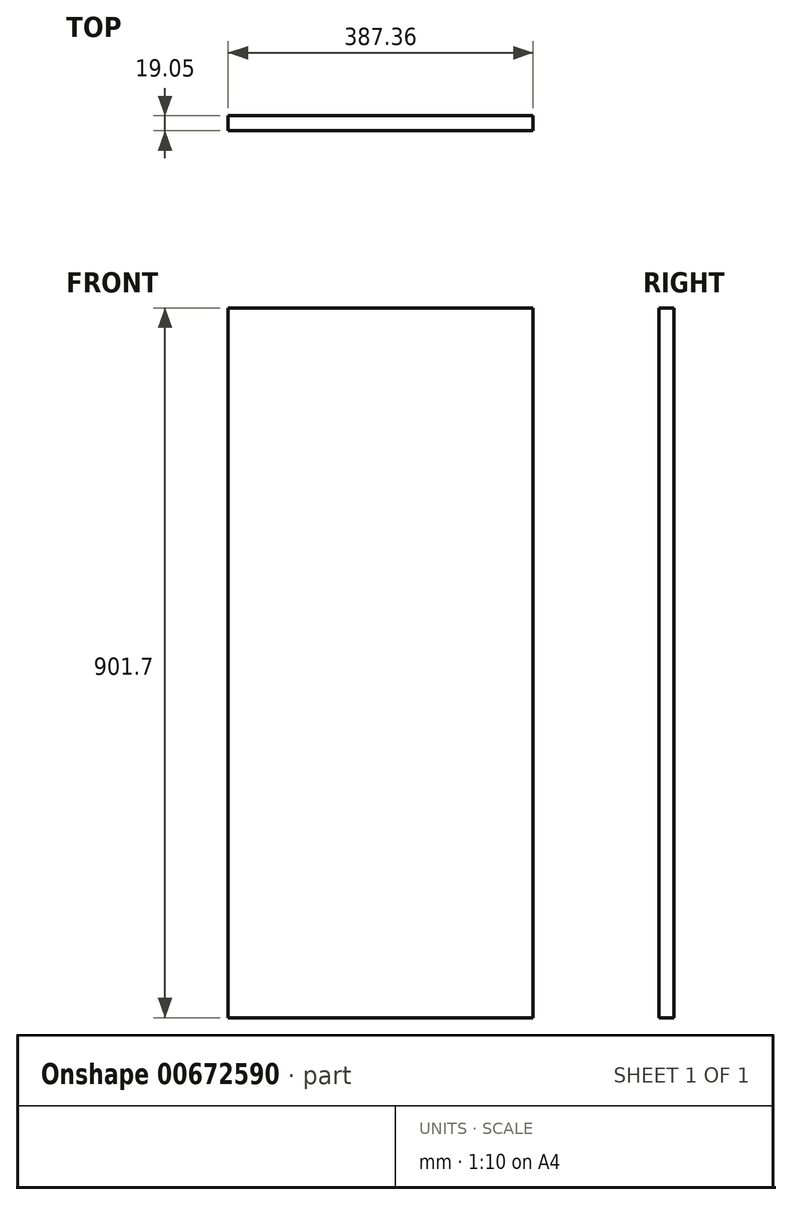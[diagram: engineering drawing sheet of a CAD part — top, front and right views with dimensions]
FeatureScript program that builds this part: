
annotation { "Feature Type Name" : "Feature", "Feature Type Description" : "" }
export const myFeature = defineFeature(function(context is Context, id is Id, definition is map)
    precondition{}
    {
        {
            var Q0;
            Q0=qCreatedBy(makeId("Front.planeOp"),FACE);
            var sketch = newSketch(context, id + "F0", { "sketchPlane" : qUnion([Q0])});
            skLineSegment(sketch, "E0.bottom", {"start": v(193.67, 450.85) * mm, "end": v(-193.68, 450.85) * mm});
            skLineSegment(sketch, "E0.top", {"start": v(193.68, -450.85) * mm, "end": v(-193.67, -450.85) * mm});
            skLineSegment(sketch, "E0.left", {"start": v(193.67, 450.85) * mm, "end": v(193.68, -450.85) * mm});
            skLineSegment(sketch, "E0.right", {"start": v(-193.68, 450.85) * mm, "end": v(-193.67, -450.85) * mm});
            skPoint(sketch, "E0.middle", {"position": v(0, 0) * mm});
            skSolve(sketch);
        }
        {
            var Q0;
            Q0=makeQuery(id+"F0.imprint","IMPRINT",FACE,{"disambiguationData":[TD([[makeQuery(id+"F0.imprint","IMPRINT",EDGE,{"derivedFrom":sQuery(id+"F0.wireOp",EDGE,"E0.bottom")}),1.0]])]});
            extrude(context, id + "F1", {"entities" : qUnion([Q0]), "depth" : 19.05 * mm, "offsetDistance" : 25.4 * mm});
        }
    });
